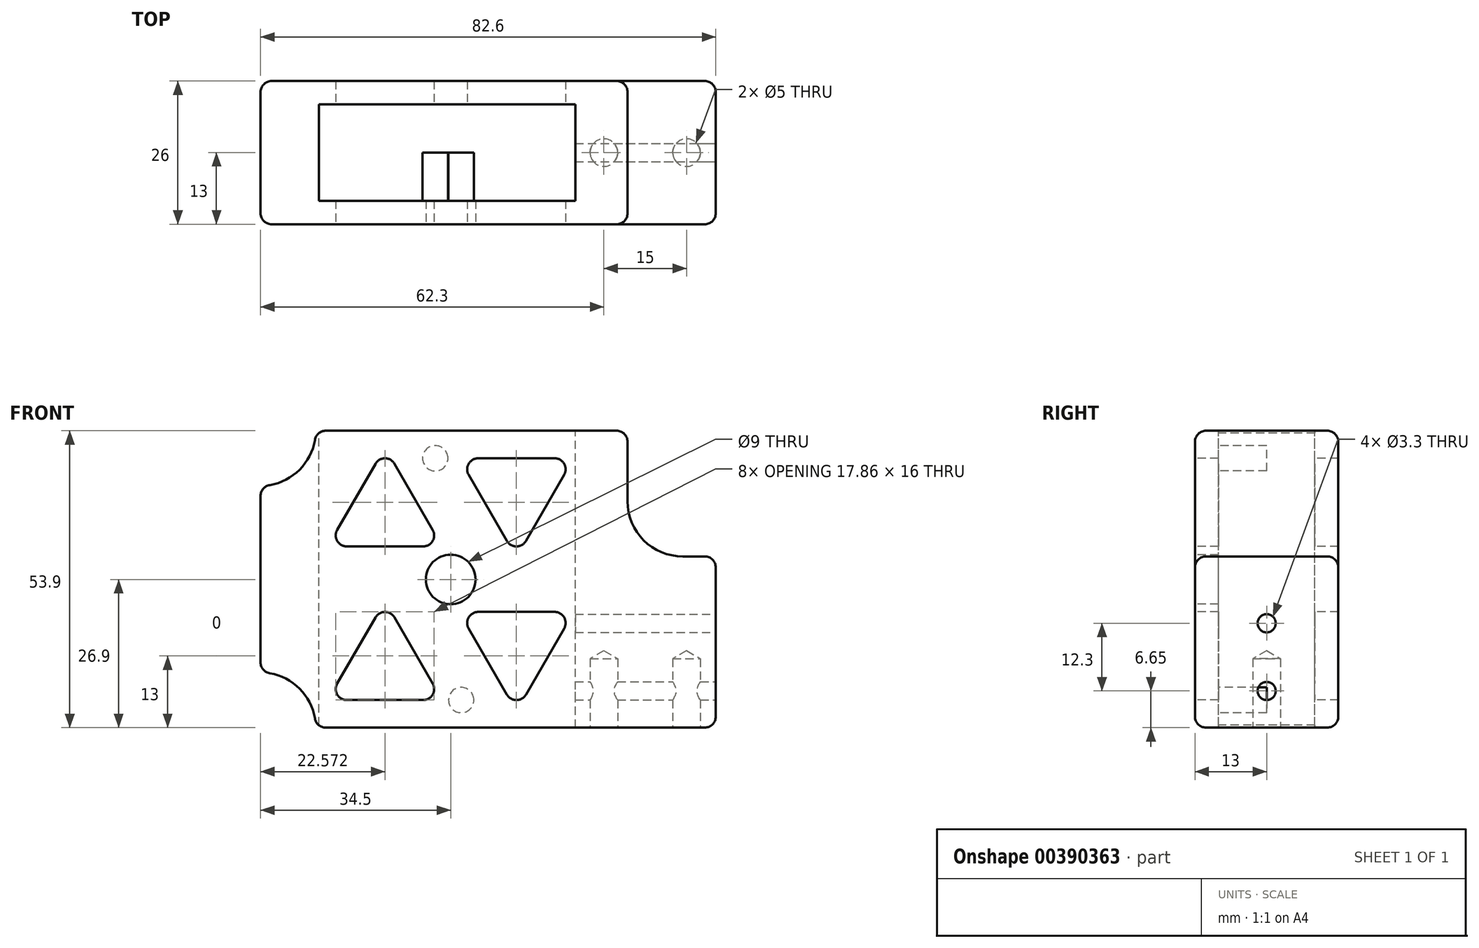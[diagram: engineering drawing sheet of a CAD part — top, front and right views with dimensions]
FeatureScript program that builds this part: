
annotation { "Feature Type Name" : "Feature", "Feature Type Description" : "" }
export const myFeature = defineFeature(function(context is Context, id is Id, definition is map)
    precondition{}
    {
        {
            var Q0;
            Q0=qCreatedBy(makeId("Front.planeOp"),FACE);
            var sketch = newSketch(context, id + "F0", { "sketchPlane" : qUnion([Q0])});
            skLineSegment(sketch, "E0.bottom", {"start": v(-29.47, 53.9) * mm, "end": v(23.3, 53.9) * mm});
            skLineSegment(sketch, "E0.top", {"start": v(-29.47, 0) * mm, "end": v(39.3, 0) * mm});
            skLineSegment(sketch, "E0.left", {"start": v(-41.3, 42.07) * mm, "end": v(-41.3, 11.83) * mm});
            skLineSegment(sketch, "E0.right", {"start": v(41.3, 29.08) * mm, "end": v(41.3, 2) * mm});
            skArc(sketch, "E1", {"start": v(-31.44, 1.67) * mm, "mid": v(-34.23, 7.07) * mm, "end": v(-39.63, 9.86) * mm});
            skArc(sketch, "E2", {"start": v(-39.63, 44.04) * mm, "mid": v(-34.23, 46.83) * mm, "end": v(-31.44, 52.23) * mm});
            skLineSegment(sketch, "E3", {"start": v(25.3, 51.9) * mm, "end": v(25.3, 41.08) * mm});
            skLineSegment(sketch, "E4", {"start": v(35.3, 31.08) * mm, "end": v(39.3, 31.08) * mm});
            skArc(sketch, "E5", {"start": v(25.3, 41.08) * mm, "mid": v(28.23, 34) * mm, "end": v(35.3, 31.08) * mm});
            skPoint(sketch, "E6.visualSharp", {"position": v(-31.3, 53.9) * mm});
            skArc(sketch, "E6.filletArc", {"start": v(-29.47, 53.9) * mm, "mid": v(-30.76, 53.43) * mm, "end": v(-31.44, 52.23) * mm});
            skPoint(sketch, "E7.visualSharp", {"position": v(-41.3, 43.9) * mm});
            skArc(sketch, "E7.filletArc", {"start": v(-39.63, 44.04) * mm, "mid": v(-40.83, 43.36) * mm, "end": v(-41.3, 42.07) * mm});
            skPoint(sketch, "E8.visualSharp", {"position": v(-41.3, 10) * mm});
            skArc(sketch, "E8.filletArc", {"start": v(-41.3, 11.83) * mm, "mid": v(-40.83, 10.54) * mm, "end": v(-39.63, 9.86) * mm});
            skPoint(sketch, "E9.visualSharp", {"position": v(-31.3, 0) * mm});
            skArc(sketch, "E9.filletArc", {"start": v(-31.44, 1.67) * mm, "mid": v(-30.76, 0.47) * mm, "end": v(-29.47, 0) * mm});
            skPoint(sketch, "E10.visualSharp", {"position": v(41.3, 0) * mm});
            skArc(sketch, "E10.filletArc", {"start": v(39.3, 0) * mm, "mid": v(40.71, 0.59) * mm, "end": v(41.3, 2) * mm});
            skPoint(sketch, "E11.orphan", {"position": v(41.3, 53.9) * mm});
            skPoint(sketch, "E12.visualSharp", {"position": v(25.3, 53.9) * mm});
            skArc(sketch, "E12.filletArc", {"start": v(25.3, 51.9) * mm, "mid": v(24.71, 53.31) * mm, "end": v(23.3, 53.9) * mm});
            skPoint(sketch, "E13.visualSharp", {"position": v(41.3, 31.08) * mm});
            skArc(sketch, "E13.filletArc", {"start": v(41.3, 29.08) * mm, "mid": v(40.71, 30.5) * mm, "end": v(39.3, 31.08) * mm});
            skSolve(sketch);
        }
        {
            var Q0;
            Q0 = qSketchRegion(id + "F0", true);
            extrude(context, id + "F1", {"entities" : qUnion([Q0]), "oppositeDirection" : true, "depth" : 26 * mm});
        }
        {
            var Q0;
            Q0=makeQuery(id+"F1.opExtrude","SWEPT_FACE",FACE,{"disambiguationData":[OSD([sQuery(id+"F0.wireOp",EDGE,"E0.bottom")])]});
            var sketch = newSketch(context, id + "F2", { "sketchPlane" : qUnion([Q0])});
            skLineSegment(sketch, "E14.bottom", {"start": v(-30.72, 21.75) * mm, "end": v(15.8, 21.75) * mm});
            skLineSegment(sketch, "E14.top", {"start": v(-30.72, 4.25) * mm, "end": v(15.8, 4.25) * mm});
            skLineSegment(sketch, "E14.left", {"start": v(-30.72, 21.75) * mm, "end": v(-30.72, 4.25) * mm});
            skLineSegment(sketch, "E14.right", {"start": v(15.8, 21.75) * mm, "end": v(15.8, 4.25) * mm});
            skSolve(sketch);
        }
        {
            var Q0;
            Q0 = qSketchRegion(id + "F2", true);
            extrude(context, id + "F3", {"entities" : qUnion([Q0]), "operationType" : NewBodyOperationType.REMOVE, "endBound" : BoundingType.THROUGH_ALL, "oppositeDirection" : true, "depth" : 25 * mm});
        }
        {
            var Q0;
            Q0=makeQuery(id+"F1.opExtrude","CAP_FACE",FACE,{"disambiguationData":[OSD([sQuery(id+"F0.wireOp",EDGE,"E0.bottom"),sQuery(id+"F0.wireOp",EDGE,"E0.top"),sQuery(id+"F0.wireOp",EDGE,"E0.left"),sQuery(id+"F0.wireOp",EDGE,"E0.right"),sQuery(id+"F0.wireOp",EDGE,"E1"),sQuery(id+"F0.wireOp",EDGE,"E2"),sQuery(id+"F0.wireOp",EDGE,"E3"),sQuery(id+"F0.wireOp",EDGE,"E4"),sQuery(id+"F0.wireOp",EDGE,"E5"),sQuery(id+"F0.wireOp",EDGE,"E6.filletArc"),sQuery(id+"F0.wireOp",EDGE,"E7.filletArc"),sQuery(id+"F0.wireOp",EDGE,"E8.filletArc"),sQuery(id+"F0.wireOp",EDGE,"E9.filletArc"),sQuery(id+"F0.wireOp",EDGE,"E10.filletArc"),sQuery(id+"F0.wireOp",EDGE,"E12.filletArc"),sQuery(id+"F0.wireOp",EDGE,"E13.filletArc")])],"isStart":true});
            var sketch = newSketch(context, id + "F4", { "sketchPlane" : qUnion([Q0])});
            skPoint(sketch, "E15", {"position": v(-6.8, 26.9) * mm});
            skSolve(sketch);
        }
        {
            var Q0;
            Q0=sQuery(id+"F4.wireOp",VERTEX,"E15");
            var Q1;
            Q1=makeQuery(id+"F1.opExtrude","SWEPT_BODY",BODY,{"disambiguationData":[OSD([sQuery(id+"F0.wireOp",EDGE,"E0.bottom"),sQuery(id+"F0.wireOp",EDGE,"E0.top"),sQuery(id+"F0.wireOp",EDGE,"E0.left"),sQuery(id+"F0.wireOp",EDGE,"E0.right"),sQuery(id+"F0.wireOp",EDGE,"E1"),sQuery(id+"F0.wireOp",EDGE,"E2"),sQuery(id+"F0.wireOp",EDGE,"E3"),sQuery(id+"F0.wireOp",EDGE,"E4"),sQuery(id+"F0.wireOp",EDGE,"E5"),sQuery(id+"F0.wireOp",EDGE,"E6.filletArc"),sQuery(id+"F0.wireOp",EDGE,"E7.filletArc"),sQuery(id+"F0.wireOp",EDGE,"E8.filletArc"),sQuery(id+"F0.wireOp",EDGE,"E9.filletArc"),sQuery(id+"F0.wireOp",EDGE,"E10.filletArc"),sQuery(id+"F0.wireOp",EDGE,"E12.filletArc"),sQuery(id+"F0.wireOp",EDGE,"E13.filletArc")])]});
            hole(context, id + "F5", {"style" : HoleStyle.SIMPLE, "endStyle" : HoleEndStyle.BLIND, "holeDiameter" : 9 * mm, "holeDepth" : 12 * mm, "isTappedThrough" : true, "tappedDepth" : 12 * mm, "tapClearance" : 3, "locations" : qUnion([Q0]), "scope" : qUnion([Q1])});
        }
        {
            var Q0;
            Q0=makeQuery(id+"F1.opExtrude","SWEPT_FACE",FACE,{"disambiguationData":[OSD([sQuery(id+"F0.wireOp",EDGE,"E0.right")])]});
            var sketch = newSketch(context, id + "F6", { "sketchPlane" : qUnion([Q0])});
            skPoint(sketch, "E16", {"position": v(13, 18.95) * mm});
            skPoint(sketch, "E17", {"position": v(13, 6.65) * mm});
            skSolve(sketch);
        }
        {
            var Q0;
            Q0=sQuery(id+"F6.wireOp",VERTEX,"E16");
            var Q1;
            Q1=sQuery(id+"F6.wireOp",VERTEX,"E17");
            var Q2;
            Q2=makeQuery(id+"F1.opExtrude","SWEPT_BODY",BODY,{"disambiguationData":[OSD([sQuery(id+"F0.wireOp",EDGE,"E0.bottom"),sQuery(id+"F0.wireOp",EDGE,"E0.top"),sQuery(id+"F0.wireOp",EDGE,"E0.left"),sQuery(id+"F0.wireOp",EDGE,"E0.right"),sQuery(id+"F0.wireOp",EDGE,"E1"),sQuery(id+"F0.wireOp",EDGE,"E2"),sQuery(id+"F0.wireOp",EDGE,"E3"),sQuery(id+"F0.wireOp",EDGE,"E4"),sQuery(id+"F0.wireOp",EDGE,"E5"),sQuery(id+"F0.wireOp",EDGE,"E6.filletArc"),sQuery(id+"F0.wireOp",EDGE,"E7.filletArc"),sQuery(id+"F0.wireOp",EDGE,"E8.filletArc"),sQuery(id+"F0.wireOp",EDGE,"E9.filletArc"),sQuery(id+"F0.wireOp",EDGE,"E10.filletArc"),sQuery(id+"F0.wireOp",EDGE,"E12.filletArc"),sQuery(id+"F0.wireOp",EDGE,"E13.filletArc")])]});
            hole(context, id + "F7", {"style" : HoleStyle.SIMPLE, "endStyle" : HoleEndStyle.BLIND, "standardTappedOrClearance" : lookupTablePath({ "standard" : "ISO", "engagement" : "75%", "pitch" : "0.7 mm", "size" : "M4", "type" : "Tapped" }), "standardBlindInLast" : lookupTablePath({ "standard" : "ISO", "engagement" : "75%", "pitch" : "0.7 mm", "size" : "M4", "type" : "Tapped" }), "holeDiameter" : 3.3 * mm, "showTappedDepth" : true, "holeDepth" : 30 * mm, "isTappedThrough" : true, "tappedDepth" : 27.9 * mm, "tapClearance" : 3, "locations" : qUnion([Q0, Q1]), "scope" : qUnion([Q2]), "majorDiameter" : 4 * mm});
        }
        {
            var Q0;
            Q0=makeQuery(id+"F1.opExtrude","SWEPT_FACE",FACE,{"disambiguationData":[OSD([sQuery(id+"F0.wireOp",EDGE,"E0.top")])]});
            var sketch = newSketch(context, id + "F8", { "sketchPlane" : qUnion([Q0])});
            skPoint(sketch, "E18", {"position": v(36, -13) * mm});
            skPoint(sketch, "E18.positionSnap0", {"position": v(39.3, -13) * mm});
            skPoint(sketch, "E19", {"position": v(21, -13) * mm});
            skSolve(sketch);
        }
        {
            var Q0;
            Q0=sQuery(id+"F8.wireOp",VERTEX,"E18");
            var Q1;
            Q1=sQuery(id+"F8.wireOp",VERTEX,"E19");
            var Q2;
            Q2=makeQuery(id+"F1.opExtrude","SWEPT_BODY",BODY,{"disambiguationData":[OSD([sQuery(id+"F0.wireOp",EDGE,"E0.bottom"),sQuery(id+"F0.wireOp",EDGE,"E0.top"),sQuery(id+"F0.wireOp",EDGE,"E0.left"),sQuery(id+"F0.wireOp",EDGE,"E0.right"),sQuery(id+"F0.wireOp",EDGE,"E1"),sQuery(id+"F0.wireOp",EDGE,"E2"),sQuery(id+"F0.wireOp",EDGE,"E3"),sQuery(id+"F0.wireOp",EDGE,"E4"),sQuery(id+"F0.wireOp",EDGE,"E5"),sQuery(id+"F0.wireOp",EDGE,"E6.filletArc"),sQuery(id+"F0.wireOp",EDGE,"E7.filletArc"),sQuery(id+"F0.wireOp",EDGE,"E8.filletArc"),sQuery(id+"F0.wireOp",EDGE,"E9.filletArc"),sQuery(id+"F0.wireOp",EDGE,"E10.filletArc"),sQuery(id+"F0.wireOp",EDGE,"E12.filletArc"),sQuery(id+"F0.wireOp",EDGE,"E13.filletArc")])]});
            hole(context, id + "F9", {"style" : HoleStyle.SIMPLE, "endStyle" : HoleEndStyle.BLIND, "standardTappedOrClearance" : lookupTablePath({ "standard" : "ISO", "engagement" : "75%", "pitch" : "1 mm", "size" : "M6", "type" : "Tapped" }), "standardBlindInLast" : lookupTablePath({ "standard" : "ISO", "engagement" : "75%", "pitch" : "1 mm", "size" : "M6", "type" : "Tapped" }), "holeDiameter" : 5 * mm, "showTappedDepth" : true, "holeDepth" : 12.5 * mm, "isTappedThrough" : true, "tappedDepth" : 9.5 * mm, "tapClearance" : 3, "locations" : qUnion([Q0, Q1]), "scope" : qUnion([Q2]), "majorDiameter" : 6 * mm});
        }
        {
            var Q0;
            Q0=makeQuery(id+"F1.opExtrude","CAP_FACE",FACE,{"disambiguationData":[OSD([sQuery(id+"F0.wireOp",EDGE,"E0.bottom"),sQuery(id+"F0.wireOp",EDGE,"E0.top"),sQuery(id+"F0.wireOp",EDGE,"E0.left"),sQuery(id+"F0.wireOp",EDGE,"E0.right"),sQuery(id+"F0.wireOp",EDGE,"E1"),sQuery(id+"F0.wireOp",EDGE,"E2"),sQuery(id+"F0.wireOp",EDGE,"E3"),sQuery(id+"F0.wireOp",EDGE,"E4"),sQuery(id+"F0.wireOp",EDGE,"E5"),sQuery(id+"F0.wireOp",EDGE,"E6.filletArc"),sQuery(id+"F0.wireOp",EDGE,"E7.filletArc"),sQuery(id+"F0.wireOp",EDGE,"E8.filletArc"),sQuery(id+"F0.wireOp",EDGE,"E9.filletArc"),sQuery(id+"F0.wireOp",EDGE,"E10.filletArc"),sQuery(id+"F0.wireOp",EDGE,"E12.filletArc"),sQuery(id+"F0.wireOp",EDGE,"E13.filletArc")])],"isStart":true});
            var sketch = newSketch(context, id + "F10", { "sketchPlane" : qUnion([Q0])});
            skCircle(sketch, "E20", {"center": v(-9.6, 48.9) * mm, "radius": 2.3 * mm});
            skCircle(sketch, "E21", {"center": v(-4.9, 5) * mm, "radius": 2.3 * mm});
            skLineSegment(sketch, "E22", {"start": v(-66.21, 51.2) * mm, "end": v(48.12, 51.2) * mm, "construction": true});
            skLineSegment(sketch, "E23", {"start": v(-60.61, 2.7) * mm, "end": v(50.15, 2.7) * mm, "construction": true});
            skLineSegment(sketch, "E24", {"start": v(-9.6, 48.9) * mm, "end": v(-9.6, 53.9) * mm, "construction": true});
            skLineSegment(sketch, "E25", {"start": v(-4.9, 5) * mm, "end": v(-4.9, 0) * mm, "construction": true});
            skSolve(sketch);
        }
        {
            var Q0;
            Q0=sQuery(id+"F10.wireOp",VERTEX,"E20.center");
            var Q1;
            Q1=sQuery(id+"F10.wireOp",VERTEX,"E25.start");
            var Q2;
            Q2=makeQuery(id+"F1.opExtrude","SWEPT_BODY",BODY,{"disambiguationData":[OSD([sQuery(id+"F0.wireOp",EDGE,"E0.bottom"),sQuery(id+"F0.wireOp",EDGE,"E0.top"),sQuery(id+"F0.wireOp",EDGE,"E0.left"),sQuery(id+"F0.wireOp",EDGE,"E0.right"),sQuery(id+"F0.wireOp",EDGE,"E1"),sQuery(id+"F0.wireOp",EDGE,"E2"),sQuery(id+"F0.wireOp",EDGE,"E3"),sQuery(id+"F0.wireOp",EDGE,"E4"),sQuery(id+"F0.wireOp",EDGE,"E5"),sQuery(id+"F0.wireOp",EDGE,"E6.filletArc"),sQuery(id+"F0.wireOp",EDGE,"E7.filletArc"),sQuery(id+"F0.wireOp",EDGE,"E8.filletArc"),sQuery(id+"F0.wireOp",EDGE,"E9.filletArc"),sQuery(id+"F0.wireOp",EDGE,"E10.filletArc"),sQuery(id+"F0.wireOp",EDGE,"E12.filletArc"),sQuery(id+"F0.wireOp",EDGE,"E13.filletArc")])]});
            hole(context, id + "F11", {"style" : HoleStyle.SIMPLE, "endStyle" : HoleEndStyle.BLIND, "holeDiameter" : 4.6 * mm, "holeDepth" : 12.5 * mm, "isTappedThrough" : true, "tappedDepth" : 9.5 * mm, "tapClearance" : 3, "locations" : qUnion([Q0, Q1]), "scope" : qUnion([Q2])});
        }
        {
            var Q0;
            Q0 = qSketchRegion(id + "F10", true);
            extrude(context, id + "F12", {"entities" : qUnion([Q0]), "operationType" : NewBodyOperationType.ADD, "oppositeDirection" : true, "depth" : 13 * mm});
        }
        {
            var Q0;
            Q0=makeQuery(id+"F1.opExtrude","CAP_FACE",FACE,{"disambiguationData":[OSD([sQuery(id+"F0.wireOp",EDGE,"E0.bottom"),sQuery(id+"F0.wireOp",EDGE,"E0.top"),sQuery(id+"F0.wireOp",EDGE,"E0.left"),sQuery(id+"F0.wireOp",EDGE,"E0.right"),sQuery(id+"F0.wireOp",EDGE,"E1"),sQuery(id+"F0.wireOp",EDGE,"E2"),sQuery(id+"F0.wireOp",EDGE,"E3"),sQuery(id+"F0.wireOp",EDGE,"E4"),sQuery(id+"F0.wireOp",EDGE,"E5"),sQuery(id+"F0.wireOp",EDGE,"E6.filletArc"),sQuery(id+"F0.wireOp",EDGE,"E7.filletArc"),sQuery(id+"F0.wireOp",EDGE,"E8.filletArc"),sQuery(id+"F0.wireOp",EDGE,"E9.filletArc"),sQuery(id+"F0.wireOp",EDGE,"E10.filletArc"),sQuery(id+"F0.wireOp",EDGE,"E12.filletArc"),sQuery(id+"F0.wireOp",EDGE,"E13.filletArc")])],"isStart":true});
            var sketch = newSketch(context, id + "F13", { "sketchPlane" : qUnion([Q0])});
            skLineSegment(sketch, "E26", {"start": v(-17, 47.9) * mm, "end": v(-10.07, 35.9) * mm});
            skLineSegment(sketch, "E27", {"start": v(-11.8, 32.9) * mm, "end": v(-25.66, 32.9) * mm});
            skLineSegment(sketch, "E28", {"start": v(-27.39, 35.9) * mm, "end": v(-20.46, 47.9) * mm});
            skPoint(sketch, "E29.visualSharp", {"position": v(-18.73, 50.9) * mm});
            skArc(sketch, "E29.filletArc", {"start": v(-17, 47.9) * mm, "mid": v(-18.73, 48.9) * mm, "end": v(-20.46, 47.9) * mm});
            skArc(sketch, "E30.filletArc", {"start": v(-11.8, 32.9) * mm, "mid": v(-10.07, 33.9) * mm, "end": v(-10.07, 35.9) * mm});
            skPoint(sketch, "E31.visualSharp", {"position": v(-29.12, 32.9) * mm});
            skArc(sketch, "E31.filletArc", {"start": v(-27.39, 35.9) * mm, "mid": v(-27.39, 33.9) * mm, "end": v(-25.66, 32.9) * mm});
            skLineSegment(sketch, "E32", {"start": v(-6.8, 59.95) * mm, "end": v(-6.8, -3) * mm, "construction": true});
            skLineSegment(sketch, "E33", {"start": v(-48.51, 26.9) * mm, "end": v(45.71, 26.9) * mm, "construction": true});
            skLineSegment(sketch, "E34", {"start": v(-30.72, 56.6) * mm, "end": v(-30.72, -1.77) * mm, "construction": true});
            skLineSegment(sketch, "E35", {"start": v(-1.8, 48.9) * mm, "end": v(12.06, 48.9) * mm});
            skLineSegment(sketch, "E36", {"start": v(13.79, 45.9) * mm, "end": v(6.86, 33.9) * mm});
            skLineSegment(sketch, "E37", {"start": v(3.4, 33.9) * mm, "end": v(-3.53, 45.9) * mm});
            skPoint(sketch, "E38.visualSharp", {"position": v(5.13, 30.9) * mm});
            skArc(sketch, "E38.filletArc", {"start": v(3.4, 33.9) * mm, "mid": v(5.13, 32.9) * mm, "end": v(6.86, 33.9) * mm});
            skPoint(sketch, "E39.visualSharp", {"position": v(15.52, 48.9) * mm});
            skArc(sketch, "E39.filletArc", {"start": v(13.79, 45.9) * mm, "mid": v(13.79, 47.9) * mm, "end": v(12.06, 48.9) * mm});
            skPoint(sketch, "E40.visualSharp", {"position": v(-5.26, 48.9) * mm});
            skArc(sketch, "E40.filletArc", {"start": v(-1.8, 48.9) * mm, "mid": v(-3.53, 47.9) * mm, "end": v(-3.53, 45.9) * mm});
            skLineSegment(sketch, "E41", {"start": v(-27.39, 8) * mm, "end": v(-20.46, 20) * mm});
            skLineSegment(sketch, "E42", {"start": v(-17, 20) * mm, "end": v(-10.07, 8) * mm});
            skLineSegment(sketch, "E43", {"start": v(-11.8, 5) * mm, "end": v(-25.66, 5) * mm});
            skPoint(sketch, "E44.visualSharp", {"position": v(-18.73, 23) * mm});
            skArc(sketch, "E44.filletArc", {"start": v(-17, 20) * mm, "mid": v(-18.73, 21) * mm, "end": v(-20.46, 20) * mm});
            skPoint(sketch, "E45.visualSharp", {"position": v(-8.34, 5) * mm});
            skArc(sketch, "E45.filletArc", {"start": v(-11.8, 5) * mm, "mid": v(-10.07, 6) * mm, "end": v(-10.07, 8) * mm});
            skPoint(sketch, "E46.visualSharp", {"position": v(-29.12, 5) * mm});
            skArc(sketch, "E46.filletArc", {"start": v(-27.39, 8) * mm, "mid": v(-27.39, 6) * mm, "end": v(-25.66, 5) * mm});
            skLineSegment(sketch, "E47", {"start": v(-3.53, 18) * mm, "end": v(3.4, 6) * mm});
            skLineSegment(sketch, "E48", {"start": v(6.86, 6) * mm, "end": v(13.79, 18) * mm});
            skLineSegment(sketch, "E49", {"start": v(12.06, 21) * mm, "end": v(-1.8, 21) * mm});
            skPoint(sketch, "E50.visualSharp", {"position": v(-5.26, 21) * mm});
            skArc(sketch, "E50.filletArc", {"start": v(-1.8, 21) * mm, "mid": v(-3.53, 20) * mm, "end": v(-3.53, 18) * mm});
            skPoint(sketch, "E51.visualSharp", {"position": v(5.13, 3) * mm});
            skArc(sketch, "E51.filletArc", {"start": v(3.4, 6) * mm, "mid": v(5.13, 5) * mm, "end": v(6.86, 6) * mm});
            skPoint(sketch, "E52.visualSharp", {"position": v(15.52, 21) * mm});
            skArc(sketch, "E52.filletArc", {"start": v(13.79, 18) * mm, "mid": v(13.79, 20) * mm, "end": v(12.06, 21) * mm});
            skSolve(sketch);
        }
        {
            var Q0;
            Q0 = qSketchRegion(id + "F13", true);
            extrude(context, id + "F14", {"entities" : qUnion([Q0]), "operationType" : NewBodyOperationType.REMOVE, "endBound" : BoundingType.THROUGH_ALL, "oppositeDirection" : true, "depth" : 25 * mm});
        }
        {
            var Q0;
            Q0=makeQuery(id+"F1.opExtrude","SWEPT_FACE",FACE,{"disambiguationData":[OSD([sQuery(id+"F0.wireOp",EDGE,"E0.left")])]});
            fillet(context, id + "F15", {"entities" : qUnion([Q0]), "radius" : 2 * mm, "tangentPropagation" : true, "allowEdgeOverflow" : false});
        }
    });
